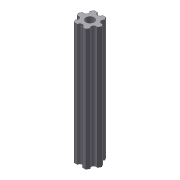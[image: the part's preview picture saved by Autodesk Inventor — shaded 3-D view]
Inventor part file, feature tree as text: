
AUTODESK INVENTOR PART (.ipt)
format: ipt  version: 2012 (Build 160160000, 160)  size: 96,256 bytes
history: native  units: in
note: dims shown in document units (in); Inventor stores cm internally (conversion verified against a paired STEP export)
features: extrude x2, sketch x2, pattern_circular x1
ambient origin geometry x8: Origin, YZ Plane, XZ Plane, XY Plane, X Axis, Y Axis, Z Axis, Center Point
bodies: Solid1 (feature_tree)
feature tree (5):
  extrude  "Extrusion1"  Depth=0.2in
  extrude  "Extrusion2"  Depth=0.0625in
  pattern_circular  "Circular Pattern1"  [2 undecoded]
  sketch  "Sketch1"  dims[d0=0.5in d1=0.2in]
  sketch  "Sketch2"  dims[d2=3.0in d3=0.0in d4=0.0625in d5=3.0in d6=0.0in d7=2.3622in d8=360.0deg]
note: 2 required parameter values undecoded (feature->parameter linkage not recoverable at this tier; creation-order binding heuristic only, values carry confidence <= 0.55)
